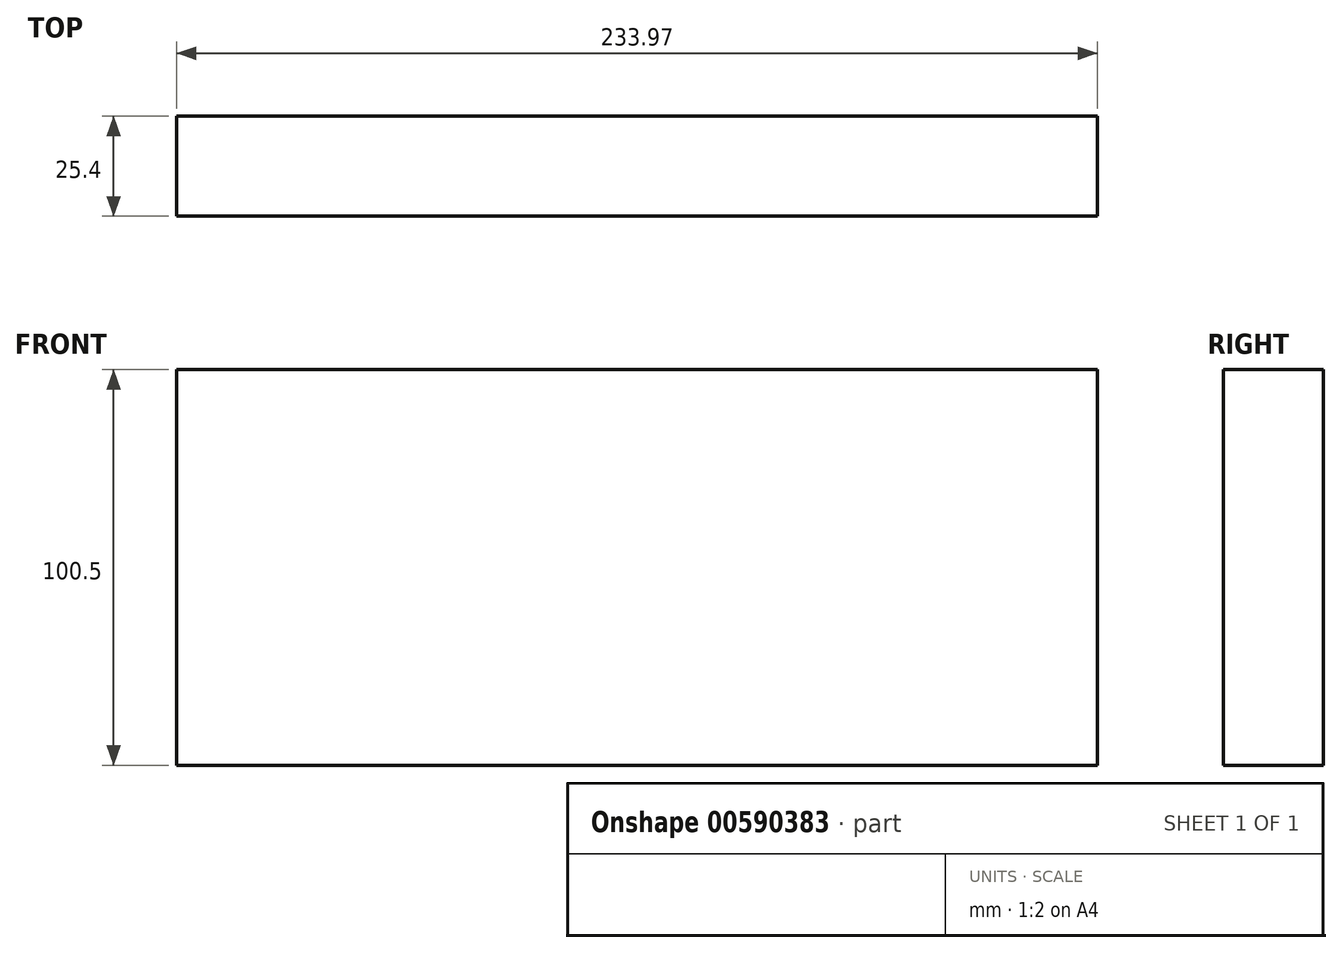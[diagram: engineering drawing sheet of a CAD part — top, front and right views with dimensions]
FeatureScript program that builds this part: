
annotation { "Feature Type Name" : "Feature", "Feature Type Description" : "" }
export const myFeature = defineFeature(function(context is Context, id is Id, definition is map)
    precondition{}
    {
        {
            var Q0;
            Q0=qCreatedBy(makeId("Front.planeOp"),FACE);
            var sketch = newSketch(context, id + "F0", { "sketchPlane" : qUnion([Q0])});
            skLineSegment(sketch, "E0.bottom", {"start": v(-196.9, 10.27) * mm, "end": v(37.06, 10.27) * mm});
            skLineSegment(sketch, "E0.top", {"start": v(-196.9, -90.23) * mm, "end": v(37.06, -90.23) * mm});
            skLineSegment(sketch, "E0.left", {"start": v(-196.9, 10.27) * mm, "end": v(-196.9, -90.23) * mm});
            skLineSegment(sketch, "E0.right", {"start": v(37.06, 10.27) * mm, "end": v(37.06, -90.23) * mm});
            skSolve(sketch);
        }
        {
            var Q0;
            Q0=makeQuery(id+"F0.imprint","IMPRINT",FACE,{"disambiguationData":[TD([[makeQuery(id+"F0.imprint","IMPRINT",EDGE,{"derivedFrom":sQuery(id+"F0.wireOp",EDGE,"E0.bottom")}),-1.0]])]});
            extrude(context, id + "F1", {"entities" : qUnion([Q0]), "depth" : 25.4 * mm, "offsetDistance" : 25.4 * mm});
        }
        {
            var Q0;
            Q0=qCreatedBy(makeId("Front.planeOp"),FACE);
            var sketch = newSketch(context, id + "F2", { "sketchPlane" : qUnion([Q0])});
            skLineSegment(sketch, "E1", {"start": v(36.92, -91.29) * mm, "end": v(96.54, -160.05) * mm});
            skLineSegment(sketch, "E2", {"start": v(36.92, 7.8) * mm, "end": v(96.54, -62.4) * mm});
            skLineSegment(sketch, "E3", {"start": v(-195.9, 8.95) * mm, "end": v(-148.36, -62.4) * mm});
            skLineSegment(sketch, "E4", {"start": v(-193.88, -90.32) * mm, "end": v(-156.2, -146.9) * mm});
            skSolve(sketch);
        }
        {
            var Q0;
            Q0=sQuery(id+"F2.wireOp",EDGE,"E4");
            extrude(context, id + "F3", {"bodyType" : ToolBodyType.SURFACE, "surfaceEntities" : qUnion([Q0]), "depth" : 25.4 * mm, "offsetDistance" : 25.4 * mm});
        }
    });
